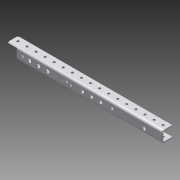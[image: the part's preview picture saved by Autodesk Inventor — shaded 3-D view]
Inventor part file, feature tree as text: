
AUTODESK INVENTOR PART (.ipt)
format: ipt  version: 2015 SP1 (Build 190203100, 203)  size: 294,912 bytes
history: native  units: in
note: dims shown in document units (in); Inventor stores cm internally (conversion verified against a paired STEP export)
features: projected_geometry x9, sketch x3, other x2, extrude x2, hole x1, imported_body x1
ambient origin geometry x8: Origin, YZ Plane, XZ Plane, XY Plane, X Axis, Y Axis, Z Axis, Center Point
bodies: Body1 (feature_tree)
feature tree (18):
  other  "Cut-Extrude6"
  other  "C-Channel 2.ipt1"
  extrude  "Extrusion1"  Depth=0.6875in
  hole  "Hole1"  [1 undecoded]
  extrude  "Extrusion2"  Depth=1.125in
  imported_body  "Base1"
  sketch  "Sketch1"  dims[d0=13.0in d1=0.0in d2=0.6875in]
  projected_geometry  "Projected Loop1"
  projected_geometry  "Projected Loop2"
  projected_geometry  "Projected Loop3"
  projected_geometry  "Projected Loop4"
  projected_geometry  "Projected Loop5"
  projected_geometry  "Projected Loop6"
  sketch  "Sketch2"  dims[d3=0.6875in d4=1.625in]
  projected_geometry  "Projected Loop7"
  projected_geometry  "Projected Loop8"
  sketch  "Sketch3"  dims[d5=6.5in d6=0.25in d7=0.75in d8=0.375in d9=0.25in d10=0.5635in d11=1.0in d12=0.8108in d13=1.125in d14=1.125in d15=1.0in d16=0.0in]
  projected_geometry  "Projected Loop9"
note: 1 required parameter value undecoded (feature->parameter linkage not recoverable at this tier; creation-order binding heuristic only, values carry confidence <= 0.55)
